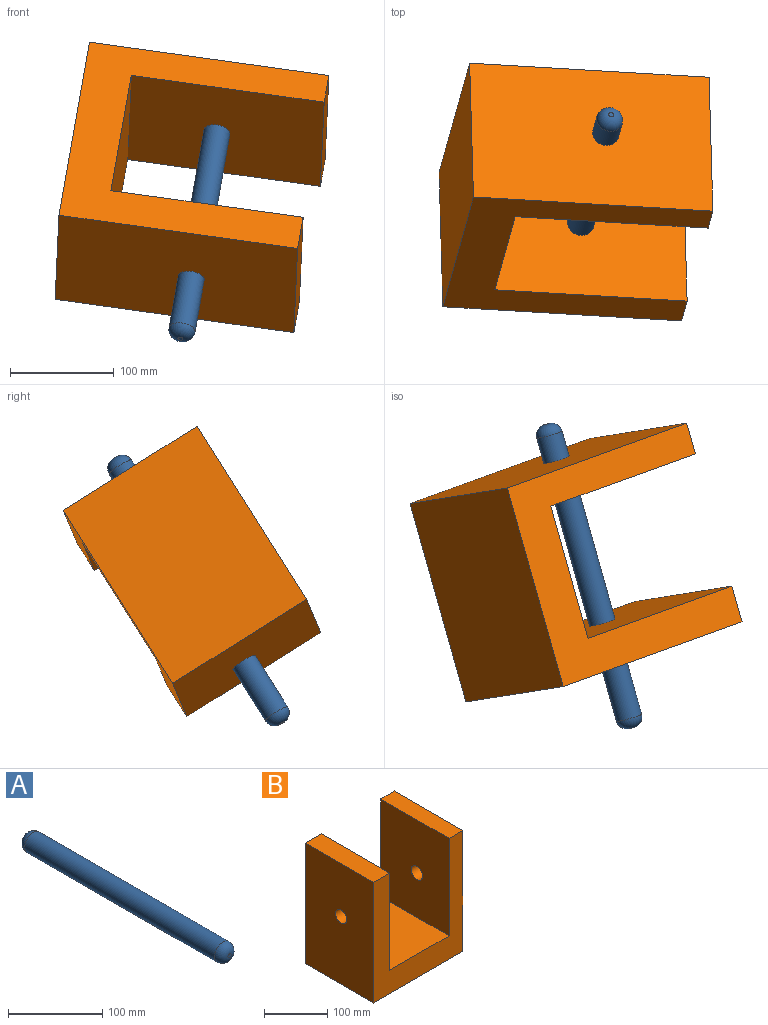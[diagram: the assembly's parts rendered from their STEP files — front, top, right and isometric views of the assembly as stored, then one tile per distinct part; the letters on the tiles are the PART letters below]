
ASSEMBLY  parts=2 mates=1
PART A: 5 faces, bbox 25.2x304.8x25.2 mm
  f0: cylinder r=12.62mm len=284.48mm, axis (0,1,0), area 22558.2mm2, adj f3,f4
  f1: plane 4.92x4.92mm, normal (0,-1,0), area 19mm2, adj f4
  f2: plane 4.92x4.92mm, normal (0,1,0), area 19mm2, adj f3
  f3: torus R=2.46mm, axis (0,-1,0), area 895.3mm2, adj f0,f2
  f4: torus R=2.46mm, axis (0,-1,0), area 895.3mm2, adj f0,f1
PART B: 12 faces, bbox 199.4x152.4x233.2 mm
  f0: plane 152.4x35.85mm, normal (0,0,1), area 5463.9mm2, adj f1,f7,f8,f9
  f1: plane 232.51x152.4mm, normal (-1,0,0), area 34928.5mm2, adj f0,f2,f8,f9,f10
  f2: plane 199.43x152.4mm, normal (0,0,-1), area 30393.1mm2, adj f1,f3,f8,f9
  f3: plane 233.21x152.4mm, normal (1,0,0), area 35034.3mm2, adj f2,f4,f8,f9,f11
  f4: plane 152.4x30.84mm, normal (0,0,1), area 4700.2mm2, adj f3,f5,f8,f9
  f5: plane 187.9x152.4mm, normal (-1,0,0), area 28129.3mm2, adj f4,f6,f8,f9,f11
  f6: plane 152.4x132.74mm, normal (0,0,1), area 20229.1mm2, adj f5,f7,f8,f9
  f7: plane 187.21x152.4mm, normal (1,0,0), area 28023.5mm2, adj f0,f6,f8,f9,f10
  f8: plane 233.21x199.43mm, normal (0,-1,0), area 21542.6mm2, adj f0,f1,f2,f3,f4,f5,f6,f7
  f9: plane 233.21x199.43mm, normal (0,1,0), area 21542.6mm2, adj f0,f1,f2,f3,f4,f5,f6,f7
  f10: cylinder r=12.7mm len=35.85mm, axis (1,0,0), area 2860.9mm2, adj f1,f7
  f11: cylinder r=12.7mm len=30.84mm, axis (1,0,0), area 2461mm2, adj f3,f5
PLACE A rot(axis=(0.47,0.8,0.37),108.4deg) t=(150.19,-456.84,125.67)mm
PLACE B rot(axis=(0.75,0.19,0.64),156.7deg) t=(75.49,-473.37,47.22)mm
MATE slider A.f0 <-> B.f10  axis (0.15,0.53,0.84) through (172.37,-511.55,-25.95)mm
